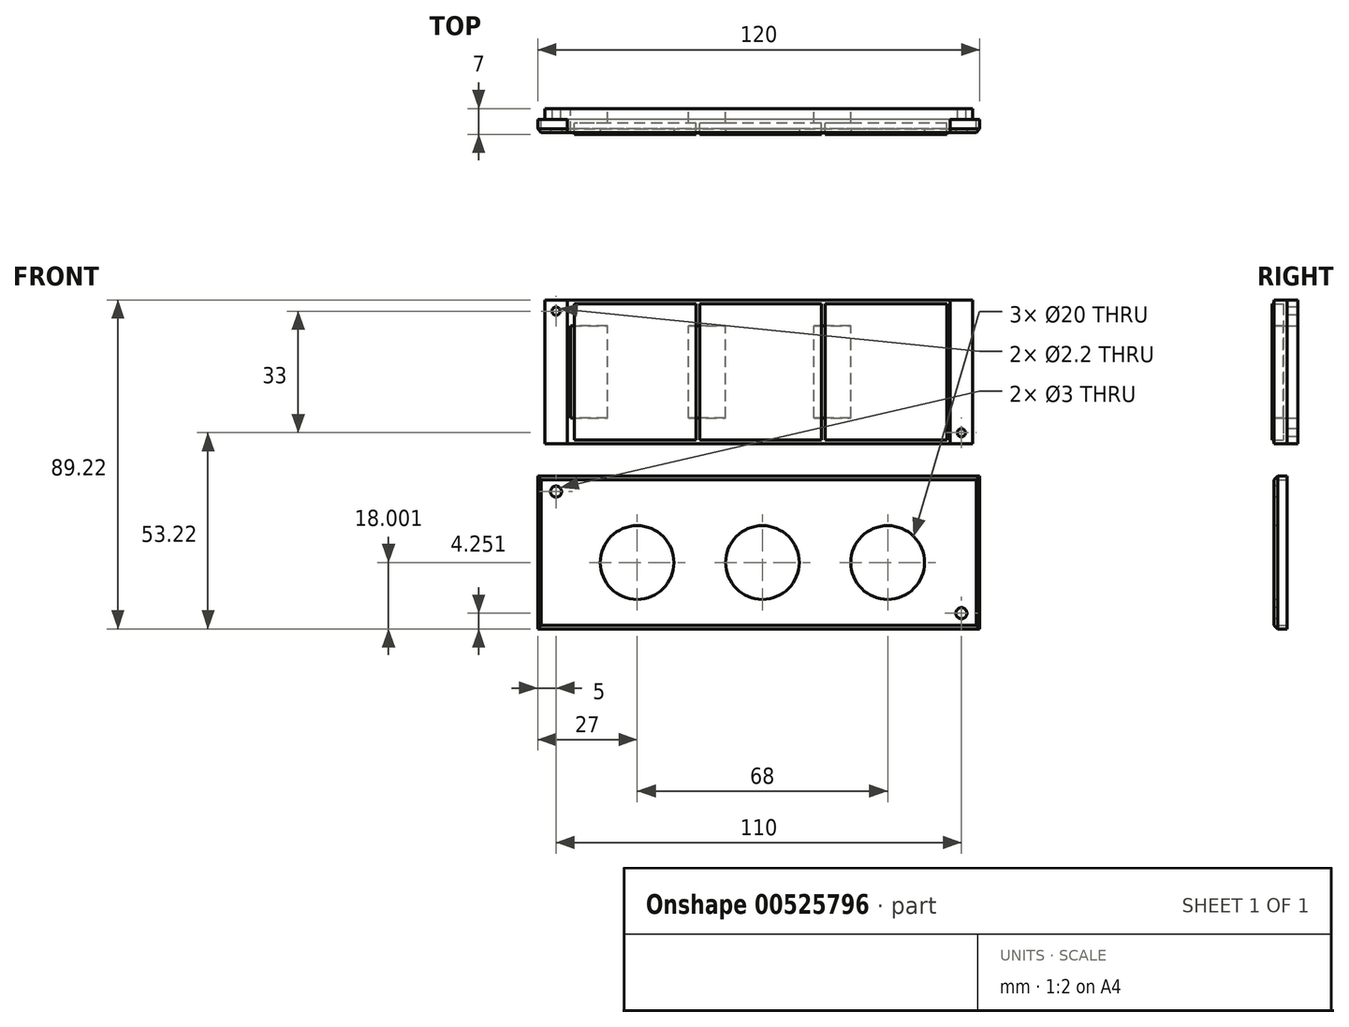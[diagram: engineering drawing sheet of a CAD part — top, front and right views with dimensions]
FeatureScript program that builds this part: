
annotation { "Feature Type Name" : "Feature", "Feature Type Description" : "" }
export const myFeature = defineFeature(function(context is Context, id is Id, definition is map)
    precondition{}
    {
        {
            var Q0;
            Q0=qCreatedBy(makeId("Front.planeOp"),FACE);
            var sketch = newSketch(context, id + "F0", { "sketchPlane" : qUnion([Q0])});
            skLineSegment(sketch, "E0.bottom", {"start": v(52, -19.5) * mm, "end": v(-52, -19.5) * mm});
            skLineSegment(sketch, "E0.top", {"start": v(52, 19.5) * mm, "end": v(-52, 19.5) * mm});
            skLineSegment(sketch, "E0.left", {"start": v(52, -19.5) * mm, "end": v(52, 19.5) * mm});
            skLineSegment(sketch, "E0.right", {"start": v(-52, -19.5) * mm, "end": v(-52, 19.5) * mm});
            skPoint(sketch, "E0.middle", {"position": v(0, 0) * mm});
            skSolve(sketch);
        }
        {
            var Q0;
            Q0=qSketchRegion(id+"F0",true);
            extrude(context, id + "F1", {"entities" : qUnion([Q0]), "depth" : 3.5 * mm});
        }
        {
            var Q0;
            Q0=makeQuery(id+"F1.opExtrude","CAP_FACE",FACE,{"disambiguationData":[OSD([sQuery(id+"F0.wireOp",EDGE,"E0.bottom"),sQuery(id+"F0.wireOp",EDGE,"E0.top"),sQuery(id+"F0.wireOp",EDGE,"E0.left"),sQuery(id+"F0.wireOp",EDGE,"E0.right")])],"isStart":false});
            shell(context, id + "F2", {"entities" : qUnion([Q0]), "thickness" : 1 * mm});
        }
        {
            var Q0;
            Q0=makeQuery(id+"F2.opShell","OFFSET_FACE",FACE,{"disambiguationData":[OSD([sQuery(id+"F0.wireOp",EDGE,"E0.bottom"),sQuery(id+"F0.wireOp",EDGE,"E0.top"),sQuery(id+"F0.wireOp",EDGE,"E0.left"),sQuery(id+"F0.wireOp",EDGE,"E0.right")])]});
            var sketch = newSketch(context, id + "F3", { "sketchPlane" : qUnion([Q0])});
            skLineSegment(sketch, "E1.bottom", {"start": v(-17, 18.5) * mm, "end": v(-16, 18.5) * mm});
            skLineSegment(sketch, "E1.top", {"start": v(-17, -18.5) * mm, "end": v(-16, -18.5) * mm});
            skLineSegment(sketch, "E1.left", {"start": v(-17, 18.5) * mm, "end": v(-17, -18.5) * mm});
            skLineSegment(sketch, "E1.right", {"start": v(-16, 18.5) * mm, "end": v(-16, -18.5) * mm});
            skLineSegment(sketch, "E2.bottom", {"start": v(17, 18.5) * mm, "end": v(18, 18.5) * mm});
            skLineSegment(sketch, "E2.top", {"start": v(17, -18.5) * mm, "end": v(18, -18.5) * mm});
            skLineSegment(sketch, "E2.left", {"start": v(17, 18.5) * mm, "end": v(17, -18.5) * mm});
            skLineSegment(sketch, "E2.right", {"start": v(18, 18.5) * mm, "end": v(18, -18.5) * mm});
            skLineSegment(sketch, "E3.bottom", {"start": v(-51, 18.5) * mm, "end": v(-50, 18.5) * mm});
            skLineSegment(sketch, "E3.top", {"start": v(-51, -18.5) * mm, "end": v(-50, -18.5) * mm});
            skLineSegment(sketch, "E3.left", {"start": v(-51, 18.5) * mm, "end": v(-51, -18.5) * mm});
            skLineSegment(sketch, "E3.right", {"start": v(-50, 18.5) * mm, "end": v(-50, -18.5) * mm});
            skSolve(sketch);
        }
        {
            var Q0;
            Q0=qSketchRegion(id+"F3",true);
            extrude(context, id + "F4", {"entities" : qUnion([Q0]), "operationType" : NewBodyOperationType.ADD, "depth" : 2.5 * mm});
        }
        {
            var Q0;
            Q0=makeQuery(id+"F1.opExtrude","CAP_FACE",FACE,{"disambiguationData":[OSD([sQuery(id+"F0.wireOp",EDGE,"E0.bottom"),sQuery(id+"F0.wireOp",EDGE,"E0.top"),sQuery(id+"F0.wireOp",EDGE,"E0.left"),sQuery(id+"F0.wireOp",EDGE,"E0.right")])],"isStart":true});
            var sketch = newSketch(context, id + "F5", { "sketchPlane" : qUnion([Q0])});
            skLineSegment(sketch, "E4.bottom", {"start": v(-58, 19.5) * mm, "end": v(58, 19.5) * mm});
            skLineSegment(sketch, "E4.top", {"start": v(-58, -19.5) * mm, "end": v(58, -19.5) * mm});
            skLineSegment(sketch, "E4.left", {"start": v(-58, 19.5) * mm, "end": v(-58, -19.5) * mm});
            skLineSegment(sketch, "E4.right", {"start": v(58, 19.5) * mm, "end": v(58, -19.5) * mm});
            skCircle(sketch, "E5", {"center": v(55, 16.5) * mm, "radius": 1.1 * mm});
            skCircle(sketch, "E6", {"center": v(55, -16.5) * mm, "radius": 1.1 * mm, "construction": true});
            skCircle(sketch, "E7", {"center": v(-55, 16.5) * mm, "radius": 1.1 * mm, "construction": true});
            skCircle(sketch, "E8", {"center": v(-55, -16.5) * mm, "radius": 1.1 * mm});
            skSolve(sketch);
        }
        {
            var Q0;
            Q0=qSketchRegion(id+"F5",true);
            extrude(context, id + "F6", {"entities" : qUnion([Q0]), "operationType" : NewBodyOperationType.ADD, "depth" : 3 * mm});
        }
        {
            var Q0;
            Q0=qCreatedBy(makeId("Front.planeOp"),FACE);
            var sketch = newSketch(context, id + "F7", { "sketchPlane" : qUnion([Q0])});
            skLineSegment(sketch, "E9.bottom", {"start": v(-51, 12.5) * mm, "end": v(-41, 12.5) * mm});
            skLineSegment(sketch, "E9.top", {"start": v(-51, -12.5) * mm, "end": v(-41, -12.5) * mm});
            skLineSegment(sketch, "E9.left", {"start": v(-51, 12.5) * mm, "end": v(-51, -12.5) * mm});
            skLineSegment(sketch, "E9.right", {"start": v(-41, 12.5) * mm, "end": v(-41, -12.5) * mm});
            skLineSegment(sketch, "E10.bottom", {"start": v(-19, 12.5) * mm, "end": v(-9, 12.5) * mm});
            skLineSegment(sketch, "E10.top", {"start": v(-19, -12.5) * mm, "end": v(-9, -12.5) * mm});
            skLineSegment(sketch, "E10.left", {"start": v(-19, 12.5) * mm, "end": v(-19, -12.5) * mm});
            skLineSegment(sketch, "E10.right", {"start": v(-9, 12.5) * mm, "end": v(-9, -12.5) * mm});
            skLineSegment(sketch, "E11.bottom", {"start": v(15, 12.5) * mm, "end": v(25, 12.5) * mm});
            skLineSegment(sketch, "E11.top", {"start": v(15, -12.5) * mm, "end": v(25, -12.5) * mm});
            skLineSegment(sketch, "E11.left", {"start": v(15, 12.5) * mm, "end": v(15, -12.5) * mm});
            skLineSegment(sketch, "E11.right", {"start": v(25, 12.5) * mm, "end": v(25, -12.5) * mm});
            skSolve(sketch);
        }
        {
            var Q0;
            Q0=qSketchRegion(id+"F7",true);
            extrude(context, id + "F8", {"entities" : qUnion([Q0]), "operationType" : NewBodyOperationType.REMOVE, "depth" : 11.2 * mm, "symmetric" : true});
        }
        {
            var Q0;
            Q0=qCreatedBy(makeId("Front.planeOp"),FACE);
            var sketch = newSketch(context, id + "F9", { "sketchPlane" : qUnion([Q0])});
            skLineSegment(sketch, "E12.bottom", {"start": v(60, -69.72) * mm, "end": v(-60, -69.72) * mm});
            skLineSegment(sketch, "E12.top", {"start": v(60, -28.22) * mm, "end": v(-60, -28.22) * mm});
            skLineSegment(sketch, "E12.left", {"start": v(60, -69.72) * mm, "end": v(60, -28.22) * mm});
            skLineSegment(sketch, "E12.right", {"start": v(-60, -69.72) * mm, "end": v(-60, -28.22) * mm});
            skPoint(sketch, "E12.middle", {"position": v(0, -48.97) * mm});
            skSolve(sketch);
        }
        {
            var Q0;
            Q0=qSketchRegion(id+"F9",true);
            extrude(context, id + "F10", {"entities" : qUnion([Q0]), "depth" : 3.5 * mm});
        }
        {
            var Q0;
            Q0=makeQuery(id+"F10.opExtrude","CAP_FACE",FACE,{"disambiguationData":[OSD([sQuery(id+"F9.wireOp",EDGE,"E12.bottom"),sQuery(id+"F9.wireOp",EDGE,"E12.top"),sQuery(id+"F9.wireOp",EDGE,"E12.left"),sQuery(id+"F9.wireOp",EDGE,"E12.right")])],"isStart":true});
            shell(context, id + "F11", {"entities" : qUnion([Q0]), "thickness" : 1 * mm});
        }
        {
            var Q0;
            Q0=makeQuery(id+"F10.opExtrude","CAP_FACE",FACE,{"disambiguationData":[OSD([sQuery(id+"F9.wireOp",EDGE,"E12.bottom"),sQuery(id+"F9.wireOp",EDGE,"E12.top"),sQuery(id+"F9.wireOp",EDGE,"E12.left"),sQuery(id+"F9.wireOp",EDGE,"E12.right")])],"isStart":false});
            var sketch = newSketch(context, id + "F12", { "sketchPlane" : qUnion([Q0])});
            skCircle(sketch, "E13", {"center": v(55, -65.47) * mm, "radius": 1.5 * mm});
            skCircle(sketch, "E14", {"center": v(-55, -32.47) * mm, "radius": 1.5 * mm});
            skCircle(sketch, "E15", {"center": v(-33, -51.72) * mm, "radius": 10 * mm});
            skCircle(sketch, "E16", {"center": v(1, -51.72) * mm, "radius": 10 * mm});
            skCircle(sketch, "E17", {"center": v(35, -51.72) * mm, "radius": 10 * mm});
            skSolve(sketch);
        }
        {
            var Q0;
            Q0=qSketchRegion(id+"F12",true);
            extrude(context, id + "F13", {"entities" : qUnion([Q0]), "operationType" : NewBodyOperationType.REMOVE, "oppositeDirection" : true, "depth" : 1 * mm});
        }
        {
            var Q0;
            Q0=makeQuery(id+"F10.opExtrude","CAP_EDGE",EDGE,{"disambiguationData":[OSD([sQuery(id+"F9.wireOp",EDGE,"E12.top")])],"isStart":false});
            var Q1;
            Q1=makeQuery(id+"F10.opExtrude","CAP_EDGE",EDGE,{"disambiguationData":[OSD([sQuery(id+"F9.wireOp",EDGE,"E12.right")])],"isStart":false});
            var Q2;
            Q2=makeQuery(id+"F10.opExtrude","CAP_EDGE",EDGE,{"disambiguationData":[OSD([sQuery(id+"F9.wireOp",EDGE,"E12.left")])],"isStart":false});
            var Q3;
            Q3=makeQuery(id+"F10.opExtrude","CAP_EDGE",EDGE,{"disambiguationData":[OSD([sQuery(id+"F9.wireOp",EDGE,"E12.bottom")])],"isStart":false});
            chamfer(context, id + "F14", {"entities" : qUnion([Q0, Q1, Q2, Q3]), "width" : 1 * mm, "tangentPropagation" : true});
        }
        {
            var Q0;
            {var subQ0=sQuery(id+"F0.wireOp",EDGE,"E0.bottom");var subQ1=sQuery(id+"F0.wireOp",EDGE,"E0.top");Q0=makeQuery(id+"F4.boolean.opBoolean","SPLIT",FACE,{"disambiguationData":[TD([makeQuery(id+"F4.opExtrude","SWEPT_FACE",FACE,{"disambiguationData":[OSD([sQuery(id+"F3.wireOp",EDGE,"E1.left")])]})])],"derivedFrom":makeQuery(id+"F2.opShell","OFFSET_FACE",FACE,{"disambiguationData":[OSD([subQ0,subQ1,sQuery(id+"F0.wireOp",EDGE,"E0.left"),sQuery(id+"F0.wireOp",EDGE,"E0.right")])]})});}
            var sketch = newSketch(context, id + "F15", { "sketchPlane" : qUnion([Q0])});
            skLineSegment(sketch, "E18.bottom", {"start": v(-50, 18.5) * mm, "end": v(-17, 18.5) * mm});
            skLineSegment(sketch, "E18.top", {"start": v(-50, -18.5) * mm, "end": v(-17, -18.5) * mm});
            skLineSegment(sketch, "E18.left", {"start": v(-50, 18.5) * mm, "end": v(-50, -18.5) * mm});
            skLineSegment(sketch, "E18.right", {"start": v(-17, 18.5) * mm, "end": v(-17, -18.5) * mm});
            skLineSegment(sketch, "E19.0", {"start": v(17, 18.5) * mm, "end": v(-16, 18.5) * mm});
            skLineSegment(sketch, "E19.1", {"start": v(-16, 18.5) * mm, "end": v(-16, 12.5) * mm});
            skLineSegment(sketch, "E19.2", {"start": v(17, -12.5) * mm, "end": v(17, -18.5) * mm});
            skLineSegment(sketch, "E19.3", {"start": v(17, -18.5) * mm, "end": v(-16, -18.5) * mm});
            skLineSegment(sketch, "E19.4", {"start": v(51, 18.5) * mm, "end": v(18, 18.5) * mm});
            skLineSegment(sketch, "E19.5", {"start": v(18, 18.5) * mm, "end": v(18, 12.5) * mm});
            skLineSegment(sketch, "E19.6", {"start": v(51, -18.5) * mm, "end": v(51, 18.5) * mm});
            skLineSegment(sketch, "E19.7", {"start": v(51, -18.5) * mm, "end": v(18, -18.5) * mm});
            skLineSegment(sketch, "E20.bottom", {"start": v(-16, 18.5) * mm, "end": v(17, 18.5) * mm});
            skLineSegment(sketch, "E20.top", {"start": v(-16, -18.5) * mm, "end": v(17, -18.5) * mm});
            skLineSegment(sketch, "E20.left", {"start": v(-16, 18.5) * mm, "end": v(-16, -18.5) * mm});
            skLineSegment(sketch, "E20.right", {"start": v(17, 18.5) * mm, "end": v(17, -18.5) * mm});
            skLineSegment(sketch, "E21.bottom", {"start": v(18, 18.5) * mm, "end": v(51, 18.5) * mm});
            skLineSegment(sketch, "E21.top", {"start": v(18, -18.5) * mm, "end": v(51, -18.5) * mm});
            skLineSegment(sketch, "E21.left", {"start": v(18, 18.5) * mm, "end": v(18, -18.5) * mm});
            skLineSegment(sketch, "E21.right", {"start": v(51, 18.5) * mm, "end": v(51, -18.5) * mm});
            skSolve(sketch);
        }
        {
            var Q0;
            Q0 = qSketchRegion(id + "F15", true);
            extrude(context, id + "F16", {"entities" : qUnion([Q0]), "depth" : 3 * mm, "offsetDistance" : 25 * mm});
        }
    });
